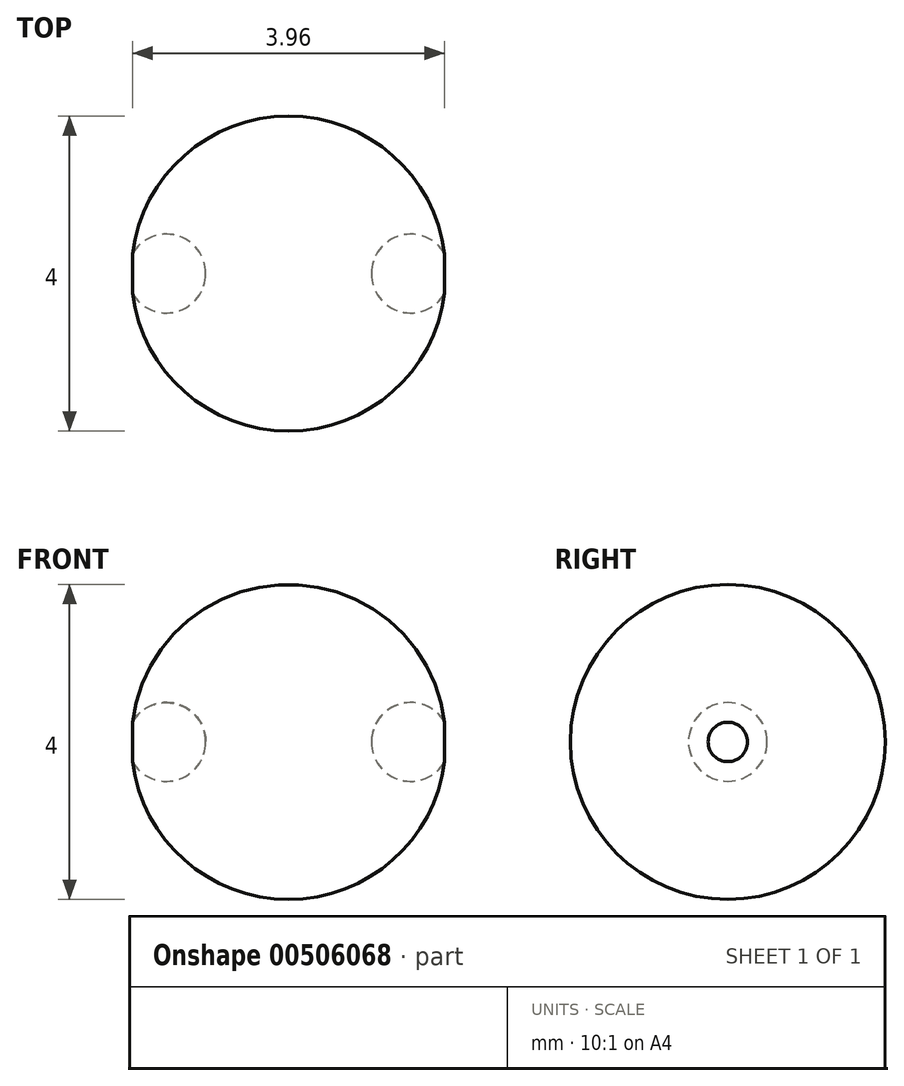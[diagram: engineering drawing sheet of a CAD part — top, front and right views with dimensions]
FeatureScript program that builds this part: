
annotation { "Feature Type Name" : "Feature", "Feature Type Description" : "" }
export const myFeature = defineFeature(function(context is Context, id is Id, definition is map)
    precondition{}
    {
        {
            var Q0;
            Q0=qCreatedBy(makeId("Front.planeOp"),FACE);
            var sketch = newSketch(context, id + "F0", { "sketchPlane" : qUnion([Q0])});
            skArc(sketch, "E0", {"start": v(0, 2) * mm, "mid": v(1.32, 1.5) * mm, "end": v(1.98, 0.25) * mm});
            skLineSegment(sketch, "E1", {"start": v(0, 2) * mm, "end": v(0, 0) * mm});
            skLineSegment(sketch, "E2", {"start": v(0, 0) * mm, "end": v(1.05, 0) * mm});
            skArc(sketch, "E3", {"start": v(1.98, 0.25) * mm, "mid": v(1.42, 0.48) * mm, "end": v(1.05, 0) * mm});
            skPoint(sketch, "E4.orphan", {"position": v(2, 0) * mm});
            skSolve(sketch);
        }
        {
            var Q0;
            Q0 = qSketchRegion(id + "F0", true);
            var Q1;
            Q1=sQuery(id+"F0.wireOp",EDGE,"E2");
            revolve(context, id + "F1", {"entities" : qUnion([Q0]), "axis" : qUnion([Q1]), "revolveType" : RevolveType.FULL});
        }
        {
            var Q0;
            Q0=makeQuery(id+"F1.opRevolve","SWEPT_BODY",BODY,{"disambiguationData":[OSD([sQuery(id+"F0.wireOp",EDGE,"E0"),sQuery(id+"F0.wireOp",EDGE,"E1"),sQuery(id+"F0.wireOp",EDGE,"E2"),sQuery(id+"F0.wireOp",EDGE,"E3")])]});
            var Q1;
            Q1=makeQuery(id+"F1.opRevolve","SWEPT_FACE",FACE,{"disambiguationData":[OSD([sQuery(id+"F0.wireOp",EDGE,"E1")])]});
            mirror(context, id + "F2", {"operationType" : NewBodyOperationType.ADD, "entities" : qUnion([Q0]), "mirrorPlane" : qUnion([Q1])});
        }
    });
